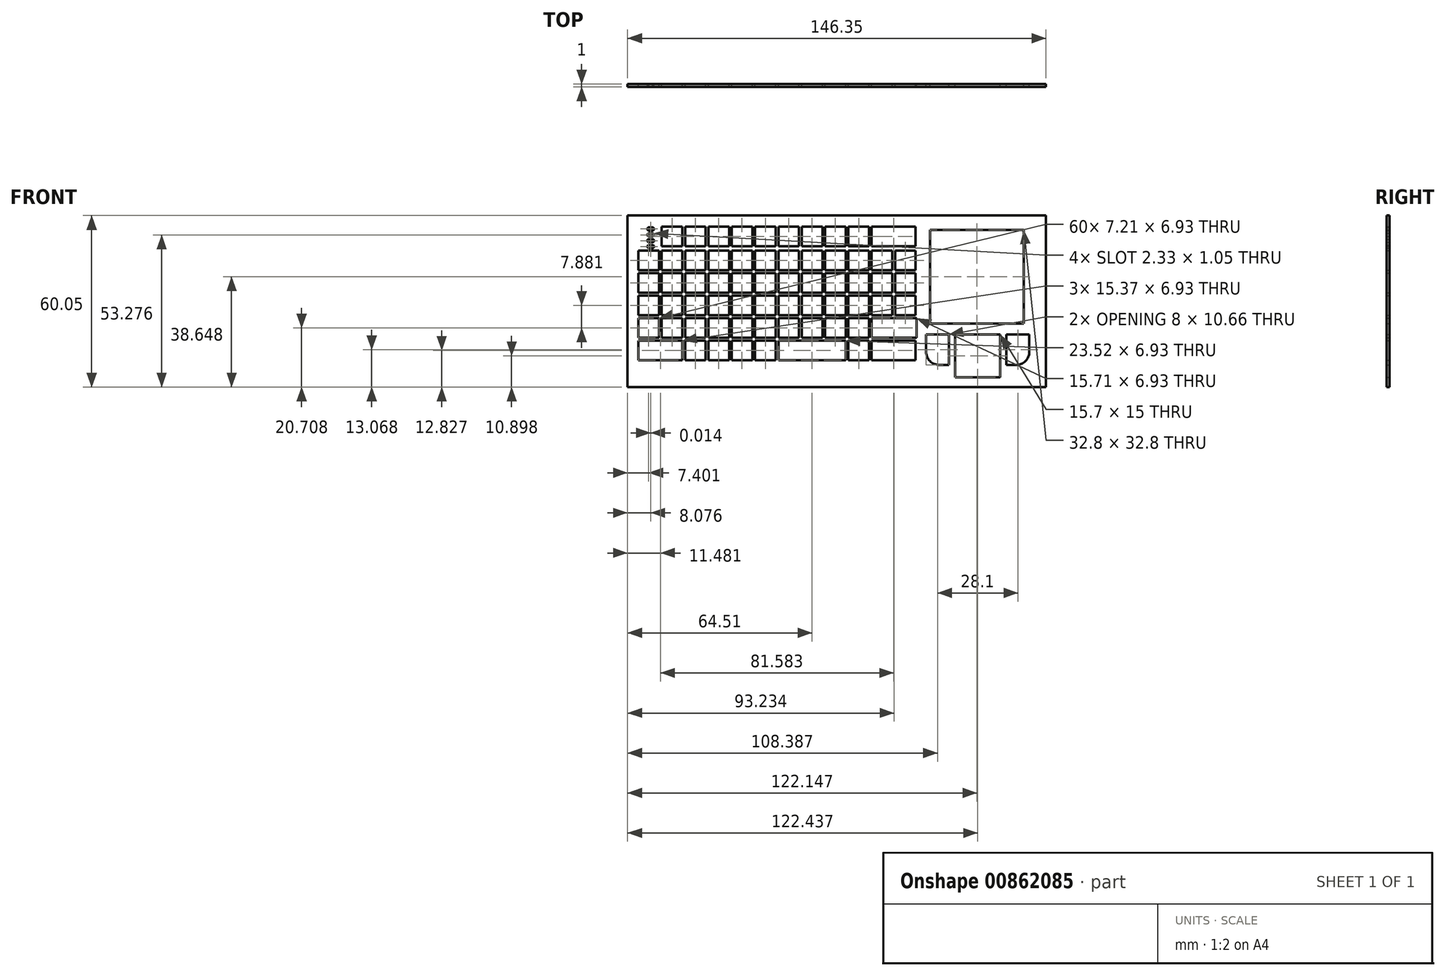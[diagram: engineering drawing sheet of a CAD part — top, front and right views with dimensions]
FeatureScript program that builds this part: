
annotation { "Feature Type Name" : "Feature", "Feature Type Description" : "" }
export const myFeature = defineFeature(function(context is Context, id is Id, definition is map)
    precondition{}
    {
        {
            var Q0;
            Q0=qCreatedBy(makeId("Front.planeOp"),FACE);
            var sketch = newSketch(context, id + "F0", { "sketchPlane" : qUnion([Q0])});
            skLineSegment(sketch, "E0.bottom", {"start": v(-58.57, 14.86) * mm, "end": v(-51.36, 14.86) * mm});
            skLineSegment(sketch, "E0.top", {"start": v(-58.57, 7.93) * mm, "end": v(-51.36, 7.93) * mm});
            skLineSegment(sketch, "E0.left", {"start": v(-58.57, 14.86) * mm, "end": v(-58.57, 7.93) * mm});
            skLineSegment(sketch, "E0.right", {"start": v(-51.36, 14.86) * mm, "end": v(-51.36, 7.93) * mm});
            skLineSegment(sketch, "E1.bottom", {"start": v(-50.41, 14.86) * mm, "end": v(-43.2, 14.86) * mm});
            skLineSegment(sketch, "E1.top", {"start": v(-50.41, 7.93) * mm, "end": v(-43.2, 7.93) * mm});
            skLineSegment(sketch, "E1.left", {"start": v(-50.41, 14.86) * mm, "end": v(-50.41, 7.93) * mm});
            skLineSegment(sketch, "E1.right", {"start": v(-43.2, 14.86) * mm, "end": v(-43.2, 7.93) * mm});
            skLineSegment(sketch, "E2.bottom", {"start": v(-42.26, 14.86) * mm, "end": v(-35.05, 14.86) * mm});
            skLineSegment(sketch, "E2.top", {"start": v(-42.26, 7.93) * mm, "end": v(-35.05, 7.93) * mm});
            skLineSegment(sketch, "E2.left", {"start": v(-42.26, 14.86) * mm, "end": v(-42.26, 7.93) * mm});
            skLineSegment(sketch, "E2.right", {"start": v(-35.05, 14.86) * mm, "end": v(-35.05, 7.93) * mm});
            skLineSegment(sketch, "E3.bottom", {"start": v(-34.1, 14.86) * mm, "end": v(-26.89, 14.86) * mm});
            skLineSegment(sketch, "E3.top", {"start": v(-34.1, 7.93) * mm, "end": v(-26.89, 7.93) * mm});
            skLineSegment(sketch, "E3.left", {"start": v(-34.1, 14.86) * mm, "end": v(-34.1, 7.93) * mm});
            skLineSegment(sketch, "E3.right", {"start": v(-26.89, 14.86) * mm, "end": v(-26.89, 7.93) * mm});
            skLineSegment(sketch, "E4.bottom", {"start": v(-25.94, 14.86) * mm, "end": v(-18.73, 14.86) * mm});
            skLineSegment(sketch, "E4.top", {"start": v(-25.94, 7.93) * mm, "end": v(-18.73, 7.93) * mm});
            skLineSegment(sketch, "E4.left", {"start": v(-25.94, 14.86) * mm, "end": v(-25.94, 7.93) * mm});
            skLineSegment(sketch, "E4.right", {"start": v(-18.73, 14.86) * mm, "end": v(-18.73, 7.93) * mm});
            skLineSegment(sketch, "E5.bottom", {"start": v(-17.78, 14.86) * mm, "end": v(-10.57, 14.86) * mm});
            skLineSegment(sketch, "E5.top", {"start": v(-17.78, 7.93) * mm, "end": v(-10.57, 7.93) * mm});
            skLineSegment(sketch, "E5.left", {"start": v(-17.78, 14.86) * mm, "end": v(-17.78, 7.93) * mm});
            skLineSegment(sketch, "E5.right", {"start": v(-10.57, 14.86) * mm, "end": v(-10.57, 7.93) * mm});
            skLineSegment(sketch, "E6.bottom", {"start": v(-9.62, 14.86) * mm, "end": v(-2.41, 14.86) * mm});
            skLineSegment(sketch, "E6.top", {"start": v(-9.62, 7.93) * mm, "end": v(-2.41, 7.93) * mm});
            skLineSegment(sketch, "E6.left", {"start": v(-9.62, 14.86) * mm, "end": v(-9.62, 7.93) * mm});
            skLineSegment(sketch, "E6.right", {"start": v(-2.41, 14.86) * mm, "end": v(-2.41, 7.93) * mm});
            skLineSegment(sketch, "E7.bottom", {"start": v(-1.46, 14.86) * mm, "end": v(5.74, 14.86) * mm});
            skLineSegment(sketch, "E7.top", {"start": v(-1.46, 7.93) * mm, "end": v(5.74, 7.93) * mm});
            skLineSegment(sketch, "E7.left", {"start": v(-1.46, 14.86) * mm, "end": v(-1.46, 7.93) * mm});
            skLineSegment(sketch, "E7.right", {"start": v(5.74, 14.86) * mm, "end": v(5.74, 7.93) * mm});
            skLineSegment(sketch, "E8.bottom", {"start": v(6.7, 14.86) * mm, "end": v(13.9, 14.86) * mm});
            skLineSegment(sketch, "E8.top", {"start": v(6.7, 7.93) * mm, "end": v(13.9, 7.93) * mm});
            skLineSegment(sketch, "E8.left", {"start": v(6.7, 14.86) * mm, "end": v(6.7, 7.93) * mm});
            skLineSegment(sketch, "E8.right", {"start": v(13.9, 14.86) * mm, "end": v(13.9, 7.93) * mm});
            skLineSegment(sketch, "E9.bottom", {"start": v(14.85, 14.86) * mm, "end": v(22.06, 14.86) * mm});
            skLineSegment(sketch, "E9.top", {"start": v(14.85, 7.93) * mm, "end": v(22.06, 7.93) * mm});
            skLineSegment(sketch, "E9.left", {"start": v(14.85, 14.86) * mm, "end": v(14.85, 7.93) * mm});
            skLineSegment(sketch, "E9.right", {"start": v(22.06, 14.86) * mm, "end": v(22.06, 7.93) * mm});
            skLineSegment(sketch, "E10.bottom", {"start": v(23.01, 14.86) * mm, "end": v(30.22, 14.86) * mm});
            skLineSegment(sketch, "E10.top", {"start": v(23.01, 7.93) * mm, "end": v(30.22, 7.93) * mm});
            skLineSegment(sketch, "E10.left", {"start": v(23.01, 14.86) * mm, "end": v(23.01, 7.93) * mm});
            skLineSegment(sketch, "E10.right", {"start": v(30.22, 14.86) * mm, "end": v(30.22, 7.93) * mm});
            skLineSegment(sketch, "E11.bottom", {"start": v(31.17, 14.86) * mm, "end": v(38.38, 14.86) * mm});
            skLineSegment(sketch, "E11.top", {"start": v(31.17, 7.93) * mm, "end": v(38.38, 7.93) * mm});
            skLineSegment(sketch, "E11.left", {"start": v(31.17, 14.86) * mm, "end": v(31.17, 7.93) * mm});
            skLineSegment(sketch, "E11.right", {"start": v(38.38, 14.86) * mm, "end": v(38.38, 7.93) * mm});
            skLineSegment(sketch, "E12", {"start": v(-58.57, 7.93) * mm, "end": v(38.38, 7.93) * mm});
            skLineSegment(sketch, "E13", {"start": v(-58.57, 14.86) * mm, "end": v(38.38, 14.86) * mm});
            skLineSegment(sketch, "E14.bottom", {"start": v(-58.57, 6.98) * mm, "end": v(-51.36, 6.98) * mm});
            skLineSegment(sketch, "E14.top", {"start": v(-58.57, 0.04) * mm, "end": v(-51.36, 0.04) * mm});
            skLineSegment(sketch, "E14.left", {"start": v(-58.57, 6.98) * mm, "end": v(-58.57, 0.04) * mm});
            skLineSegment(sketch, "E14.right", {"start": v(-51.36, 6.98) * mm, "end": v(-51.36, 0.04) * mm});
            skLineSegment(sketch, "E15.bottom", {"start": v(-50.41, 6.98) * mm, "end": v(-43.2, 6.98) * mm});
            skLineSegment(sketch, "E15.top", {"start": v(-50.41, 0.04) * mm, "end": v(-43.2, 0.04) * mm});
            skLineSegment(sketch, "E15.left", {"start": v(-50.41, 6.98) * mm, "end": v(-50.41, 0.04) * mm});
            skLineSegment(sketch, "E15.right", {"start": v(-43.2, 6.98) * mm, "end": v(-43.2, 0.04) * mm});
            skLineSegment(sketch, "E16.bottom", {"start": v(-42.26, 6.98) * mm, "end": v(-35.05, 6.98) * mm});
            skLineSegment(sketch, "E16.top", {"start": v(-42.26, 0.04) * mm, "end": v(-35.05, 0.04) * mm});
            skLineSegment(sketch, "E16.left", {"start": v(-42.26, 6.98) * mm, "end": v(-42.26, 0.04) * mm});
            skLineSegment(sketch, "E16.right", {"start": v(-35.05, 6.98) * mm, "end": v(-35.05, 0.04) * mm});
            skLineSegment(sketch, "E17.bottom", {"start": v(-34.1, 6.98) * mm, "end": v(-26.89, 6.98) * mm});
            skLineSegment(sketch, "E17.top", {"start": v(-34.1, 0.04) * mm, "end": v(-26.89, 0.04) * mm});
            skLineSegment(sketch, "E17.left", {"start": v(-34.1, 6.98) * mm, "end": v(-34.1, 0.04) * mm});
            skLineSegment(sketch, "E17.right", {"start": v(-26.89, 6.98) * mm, "end": v(-26.89, 0.04) * mm});
            skLineSegment(sketch, "E18.bottom", {"start": v(-25.94, 6.98) * mm, "end": v(-18.73, 6.98) * mm});
            skLineSegment(sketch, "E18.top", {"start": v(-25.94, 0.04) * mm, "end": v(-18.73, 0.04) * mm});
            skLineSegment(sketch, "E18.left", {"start": v(-25.94, 6.98) * mm, "end": v(-25.94, 0.04) * mm});
            skLineSegment(sketch, "E18.right", {"start": v(-18.73, 6.98) * mm, "end": v(-18.73, 0.04) * mm});
            skLineSegment(sketch, "E19.bottom", {"start": v(-17.78, 6.98) * mm, "end": v(-10.57, 6.98) * mm});
            skLineSegment(sketch, "E19.top", {"start": v(-17.78, 0.04) * mm, "end": v(-10.57, 0.04) * mm});
            skLineSegment(sketch, "E19.left", {"start": v(-17.78, 6.98) * mm, "end": v(-17.78, 0.04) * mm});
            skLineSegment(sketch, "E19.right", {"start": v(-10.57, 6.98) * mm, "end": v(-10.57, 0.04) * mm});
            skLineSegment(sketch, "E20.bottom", {"start": v(-9.62, 6.98) * mm, "end": v(-2.41, 6.98) * mm});
            skLineSegment(sketch, "E20.top", {"start": v(-9.62, 0.04) * mm, "end": v(-2.41, 0.04) * mm});
            skLineSegment(sketch, "E20.left", {"start": v(-9.62, 6.98) * mm, "end": v(-9.62, 0.04) * mm});
            skLineSegment(sketch, "E20.right", {"start": v(-2.41, 6.98) * mm, "end": v(-2.41, 0.04) * mm});
            skLineSegment(sketch, "E21.bottom", {"start": v(-1.46, 6.98) * mm, "end": v(5.74, 6.98) * mm});
            skLineSegment(sketch, "E21.top", {"start": v(-1.46, 0.04) * mm, "end": v(5.74, 0.04) * mm});
            skLineSegment(sketch, "E21.left", {"start": v(-1.46, 6.98) * mm, "end": v(-1.46, 0.04) * mm});
            skLineSegment(sketch, "E21.right", {"start": v(5.74, 6.98) * mm, "end": v(5.74, 0.04) * mm});
            skLineSegment(sketch, "E22.bottom", {"start": v(6.7, 6.98) * mm, "end": v(13.9, 6.98) * mm});
            skLineSegment(sketch, "E22.top", {"start": v(6.7, 0.04) * mm, "end": v(13.9, 0.04) * mm});
            skLineSegment(sketch, "E22.left", {"start": v(6.7, 6.98) * mm, "end": v(6.7, 0.04) * mm});
            skLineSegment(sketch, "E22.right", {"start": v(13.9, 6.98) * mm, "end": v(13.9, 0.04) * mm});
            skLineSegment(sketch, "E23.bottom", {"start": v(14.85, 6.98) * mm, "end": v(22.06, 6.98) * mm});
            skLineSegment(sketch, "E23.top", {"start": v(14.85, 0.04) * mm, "end": v(22.06, 0.04) * mm});
            skLineSegment(sketch, "E23.left", {"start": v(14.85, 6.98) * mm, "end": v(14.85, 0.04) * mm});
            skLineSegment(sketch, "E23.right", {"start": v(22.06, 6.98) * mm, "end": v(22.06, 0.04) * mm});
            skLineSegment(sketch, "E24.bottom", {"start": v(23.01, 6.98) * mm, "end": v(30.22, 6.98) * mm});
            skLineSegment(sketch, "E24.top", {"start": v(23.01, 0.04) * mm, "end": v(30.22, 0.04) * mm});
            skLineSegment(sketch, "E24.left", {"start": v(23.01, 6.98) * mm, "end": v(23.01, 0.04) * mm});
            skLineSegment(sketch, "E24.right", {"start": v(30.22, 6.98) * mm, "end": v(30.22, 0.04) * mm});
            skLineSegment(sketch, "E25.bottom", {"start": v(31.17, 6.98) * mm, "end": v(38.38, 6.98) * mm});
            skLineSegment(sketch, "E25.top", {"start": v(31.17, 0.04) * mm, "end": v(38.38, 0.04) * mm});
            skLineSegment(sketch, "E25.left", {"start": v(31.17, 6.98) * mm, "end": v(31.17, 0.04) * mm});
            skLineSegment(sketch, "E25.right", {"start": v(38.38, 6.98) * mm, "end": v(38.38, 0.04) * mm});
            skLineSegment(sketch, "E26", {"start": v(-58.57, 0.04) * mm, "end": v(38.38, 0.04) * mm});
            skLineSegment(sketch, "E27", {"start": v(-58.57, 6.98) * mm, "end": v(38.38, 6.98) * mm});
            skLineSegment(sketch, "E28.bottom", {"start": v(-58.57, -0.9) * mm, "end": v(-51.36, -0.9) * mm});
            skLineSegment(sketch, "E28.top", {"start": v(-58.57, -7.84) * mm, "end": v(-51.36, -7.84) * mm});
            skLineSegment(sketch, "E28.left", {"start": v(-58.57, -0.9) * mm, "end": v(-58.57, -7.84) * mm});
            skLineSegment(sketch, "E28.right", {"start": v(-51.36, -0.9) * mm, "end": v(-51.36, -7.84) * mm});
            skLineSegment(sketch, "E29.bottom", {"start": v(-50.41, -0.9) * mm, "end": v(-43.2, -0.9) * mm});
            skLineSegment(sketch, "E29.top", {"start": v(-50.41, -7.84) * mm, "end": v(-43.2, -7.84) * mm});
            skLineSegment(sketch, "E29.left", {"start": v(-50.41, -0.9) * mm, "end": v(-50.41, -7.84) * mm});
            skLineSegment(sketch, "E29.right", {"start": v(-43.2, -0.9) * mm, "end": v(-43.2, -7.84) * mm});
            skLineSegment(sketch, "E30.bottom", {"start": v(-42.26, -0.9) * mm, "end": v(-35.05, -0.9) * mm});
            skLineSegment(sketch, "E30.top", {"start": v(-42.26, -7.84) * mm, "end": v(-35.05, -7.84) * mm});
            skLineSegment(sketch, "E30.left", {"start": v(-42.26, -0.9) * mm, "end": v(-42.26, -7.84) * mm});
            skLineSegment(sketch, "E30.right", {"start": v(-35.05, -0.9) * mm, "end": v(-35.05, -7.84) * mm});
            skLineSegment(sketch, "E31.bottom", {"start": v(-34.1, -0.9) * mm, "end": v(-26.89, -0.9) * mm});
            skLineSegment(sketch, "E31.top", {"start": v(-34.1, -7.84) * mm, "end": v(-26.89, -7.84) * mm});
            skLineSegment(sketch, "E31.left", {"start": v(-34.1, -0.9) * mm, "end": v(-34.1, -7.84) * mm});
            skLineSegment(sketch, "E31.right", {"start": v(-26.89, -0.9) * mm, "end": v(-26.89, -7.84) * mm});
            skLineSegment(sketch, "E32.bottom", {"start": v(-25.94, -0.9) * mm, "end": v(-18.73, -0.9) * mm});
            skLineSegment(sketch, "E32.top", {"start": v(-25.94, -7.84) * mm, "end": v(-18.73, -7.84) * mm});
            skLineSegment(sketch, "E32.left", {"start": v(-25.94, -0.9) * mm, "end": v(-25.94, -7.84) * mm});
            skLineSegment(sketch, "E32.right", {"start": v(-18.73, -0.9) * mm, "end": v(-18.73, -7.84) * mm});
            skLineSegment(sketch, "E33.bottom", {"start": v(-17.78, -0.9) * mm, "end": v(-10.57, -0.9) * mm});
            skLineSegment(sketch, "E33.top", {"start": v(-17.78, -7.84) * mm, "end": v(-10.57, -7.84) * mm});
            skLineSegment(sketch, "E33.left", {"start": v(-17.78, -0.9) * mm, "end": v(-17.78, -7.84) * mm});
            skLineSegment(sketch, "E33.right", {"start": v(-10.57, -0.9) * mm, "end": v(-10.57, -7.84) * mm});
            skLineSegment(sketch, "E34.bottom", {"start": v(-9.62, -0.9) * mm, "end": v(-2.41, -0.9) * mm});
            skLineSegment(sketch, "E34.top", {"start": v(-9.62, -7.84) * mm, "end": v(-2.41, -7.84) * mm});
            skLineSegment(sketch, "E34.left", {"start": v(-9.62, -0.9) * mm, "end": v(-9.62, -7.84) * mm});
            skLineSegment(sketch, "E34.right", {"start": v(-2.41, -0.9) * mm, "end": v(-2.41, -7.84) * mm});
            skLineSegment(sketch, "E35.bottom", {"start": v(-1.46, -0.9) * mm, "end": v(5.74, -0.9) * mm});
            skLineSegment(sketch, "E35.top", {"start": v(-1.46, -7.84) * mm, "end": v(5.74, -7.84) * mm});
            skLineSegment(sketch, "E35.left", {"start": v(-1.46, -0.9) * mm, "end": v(-1.46, -7.84) * mm});
            skLineSegment(sketch, "E35.right", {"start": v(5.74, -0.9) * mm, "end": v(5.74, -7.84) * mm});
            skLineSegment(sketch, "E36.bottom", {"start": v(6.7, -0.9) * mm, "end": v(13.9, -0.9) * mm});
            skLineSegment(sketch, "E36.top", {"start": v(6.7, -7.84) * mm, "end": v(13.9, -7.84) * mm});
            skLineSegment(sketch, "E36.left", {"start": v(6.7, -0.9) * mm, "end": v(6.7, -7.84) * mm});
            skLineSegment(sketch, "E36.right", {"start": v(13.9, -0.9) * mm, "end": v(13.9, -7.84) * mm});
            skLineSegment(sketch, "E37.bottom", {"start": v(14.85, -0.9) * mm, "end": v(22.06, -0.9) * mm});
            skLineSegment(sketch, "E37.top", {"start": v(14.85, -7.84) * mm, "end": v(22.06, -7.84) * mm});
            skLineSegment(sketch, "E37.left", {"start": v(14.85, -0.9) * mm, "end": v(14.85, -7.84) * mm});
            skLineSegment(sketch, "E37.right", {"start": v(22.06, -0.9) * mm, "end": v(22.06, -7.84) * mm});
            skLineSegment(sketch, "E38.bottom", {"start": v(23.01, -0.9) * mm, "end": v(30.22, -0.9) * mm});
            skLineSegment(sketch, "E38.top", {"start": v(23.01, -7.84) * mm, "end": v(30.22, -7.84) * mm});
            skLineSegment(sketch, "E38.left", {"start": v(23.01, -0.9) * mm, "end": v(23.01, -7.84) * mm});
            skLineSegment(sketch, "E38.right", {"start": v(30.22, -0.9) * mm, "end": v(30.22, -7.84) * mm});
            skLineSegment(sketch, "E39.bottom", {"start": v(31.17, -0.9) * mm, "end": v(38.38, -0.9) * mm});
            skLineSegment(sketch, "E39.top", {"start": v(31.17, -7.84) * mm, "end": v(38.38, -7.84) * mm});
            skLineSegment(sketch, "E39.left", {"start": v(31.17, -0.9) * mm, "end": v(31.17, -7.84) * mm});
            skLineSegment(sketch, "E39.right", {"start": v(38.38, -0.9) * mm, "end": v(38.38, -7.84) * mm});
            skLineSegment(sketch, "E40", {"start": v(-58.57, -7.84) * mm, "end": v(38.38, -7.84) * mm});
            skLineSegment(sketch, "E41", {"start": v(-58.57, -0.9) * mm, "end": v(38.38, -0.9) * mm});
            skLineSegment(sketch, "E42.bottom", {"start": v(-58.57, -8.79) * mm, "end": v(-51.36, -8.79) * mm});
            skLineSegment(sketch, "E42.top", {"start": v(-58.57, -15.72) * mm, "end": v(-51.36, -15.72) * mm});
            skLineSegment(sketch, "E42.left", {"start": v(-58.57, -8.79) * mm, "end": v(-58.57, -15.72) * mm});
            skLineSegment(sketch, "E42.right", {"start": v(-51.36, -8.79) * mm, "end": v(-51.36, -15.72) * mm});
            skLineSegment(sketch, "E43.bottom", {"start": v(-50.41, -8.79) * mm, "end": v(-43.2, -8.79) * mm});
            skLineSegment(sketch, "E43.top", {"start": v(-50.41, -15.72) * mm, "end": v(-43.2, -15.72) * mm});
            skLineSegment(sketch, "E43.left", {"start": v(-50.41, -8.79) * mm, "end": v(-50.41, -15.72) * mm});
            skLineSegment(sketch, "E43.right", {"start": v(-43.2, -8.79) * mm, "end": v(-43.2, -15.72) * mm});
            skLineSegment(sketch, "E44.bottom", {"start": v(-42.26, -8.79) * mm, "end": v(-35.05, -8.79) * mm});
            skLineSegment(sketch, "E44.top", {"start": v(-42.26, -15.72) * mm, "end": v(-35.05, -15.72) * mm});
            skLineSegment(sketch, "E44.left", {"start": v(-42.26, -8.79) * mm, "end": v(-42.26, -15.72) * mm});
            skLineSegment(sketch, "E44.right", {"start": v(-35.05, -8.79) * mm, "end": v(-35.05, -15.72) * mm});
            skLineSegment(sketch, "E45.bottom", {"start": v(-34.1, -8.79) * mm, "end": v(-26.89, -8.79) * mm});
            skLineSegment(sketch, "E45.top", {"start": v(-34.1, -15.72) * mm, "end": v(-26.89, -15.72) * mm});
            skLineSegment(sketch, "E45.left", {"start": v(-34.1, -8.79) * mm, "end": v(-34.1, -15.72) * mm});
            skLineSegment(sketch, "E45.right", {"start": v(-26.89, -8.79) * mm, "end": v(-26.89, -15.72) * mm});
            skLineSegment(sketch, "E46.bottom", {"start": v(-25.94, -8.79) * mm, "end": v(-18.73, -8.79) * mm});
            skLineSegment(sketch, "E46.top", {"start": v(-25.94, -15.72) * mm, "end": v(-18.73, -15.72) * mm});
            skLineSegment(sketch, "E46.left", {"start": v(-25.94, -8.79) * mm, "end": v(-25.94, -15.72) * mm});
            skLineSegment(sketch, "E46.right", {"start": v(-18.73, -8.79) * mm, "end": v(-18.73, -15.72) * mm});
            skLineSegment(sketch, "E47.bottom", {"start": v(-17.78, -8.79) * mm, "end": v(-10.57, -8.79) * mm});
            skLineSegment(sketch, "E47.top", {"start": v(-17.78, -15.72) * mm, "end": v(-10.57, -15.72) * mm});
            skLineSegment(sketch, "E47.left", {"start": v(-17.78, -8.79) * mm, "end": v(-17.78, -15.72) * mm});
            skLineSegment(sketch, "E47.right", {"start": v(-10.57, -8.79) * mm, "end": v(-10.57, -15.72) * mm});
            skLineSegment(sketch, "E48.bottom", {"start": v(-9.62, -8.79) * mm, "end": v(-2.41, -8.79) * mm});
            skLineSegment(sketch, "E48.top", {"start": v(-9.62, -15.72) * mm, "end": v(-2.41, -15.72) * mm});
            skLineSegment(sketch, "E48.left", {"start": v(-9.62, -8.79) * mm, "end": v(-9.62, -15.72) * mm});
            skLineSegment(sketch, "E48.right", {"start": v(-2.41, -8.79) * mm, "end": v(-2.41, -15.72) * mm});
            skLineSegment(sketch, "E49.bottom", {"start": v(-1.46, -8.79) * mm, "end": v(5.74, -8.79) * mm});
            skLineSegment(sketch, "E49.top", {"start": v(-1.46, -15.72) * mm, "end": v(5.74, -15.72) * mm});
            skLineSegment(sketch, "E49.left", {"start": v(-1.46, -8.79) * mm, "end": v(-1.46, -15.72) * mm});
            skLineSegment(sketch, "E49.right", {"start": v(5.74, -8.79) * mm, "end": v(5.74, -15.72) * mm});
            skLineSegment(sketch, "E50.bottom", {"start": v(6.7, -8.79) * mm, "end": v(13.9, -8.79) * mm});
            skLineSegment(sketch, "E50.top", {"start": v(6.7, -15.72) * mm, "end": v(13.9, -15.72) * mm});
            skLineSegment(sketch, "E50.left", {"start": v(6.7, -8.79) * mm, "end": v(6.7, -15.72) * mm});
            skLineSegment(sketch, "E50.right", {"start": v(13.9, -8.79) * mm, "end": v(13.9, -15.72) * mm});
            skLineSegment(sketch, "E51.bottom", {"start": v(14.85, -8.79) * mm, "end": v(22.06, -8.79) * mm});
            skLineSegment(sketch, "E51.top", {"start": v(14.85, -15.72) * mm, "end": v(22.06, -15.72) * mm});
            skLineSegment(sketch, "E51.left", {"start": v(14.85, -8.79) * mm, "end": v(14.85, -15.72) * mm});
            skLineSegment(sketch, "E51.right", {"start": v(22.06, -8.79) * mm, "end": v(22.06, -15.72) * mm});
            skLineSegment(sketch, "E52.bottom", {"start": v(23.01, -8.79) * mm, "end": v(30.22, -8.79) * mm});
            skLineSegment(sketch, "E52.top", {"start": v(23.01, -15.72) * mm, "end": v(30.22, -15.72) * mm});
            skLineSegment(sketch, "E52.left", {"start": v(23.01, -8.79) * mm, "end": v(23.01, -15.72) * mm});
            skLineSegment(sketch, "E53.bottom", {"start": v(31.5, -8.79) * mm, "end": v(38.72, -8.79) * mm});
            skLineSegment(sketch, "E53.top", {"start": v(31.17, -15.72) * mm, "end": v(38.72, -15.72) * mm});
            skLineSegment(sketch, "E53.right", {"start": v(38.72, -8.79) * mm, "end": v(38.72, -15.72) * mm});
            skLineSegment(sketch, "E54", {"start": v(-58.57, -15.72) * mm, "end": v(38.72, -15.72) * mm});
            skLineSegment(sketch, "E55", {"start": v(-58.57, -8.79) * mm, "end": v(38.72, -8.79) * mm});
            skLineSegment(sketch, "E56.bottom", {"start": v(-58.57, -16.67) * mm, "end": v(-51.36, -16.67) * mm});
            skLineSegment(sketch, "E56.top", {"start": v(-56.77, -23.6) * mm, "end": v(-51.36, -23.6) * mm});
            skLineSegment(sketch, "E56.left", {"start": v(-58.57, -16.67) * mm, "end": v(-58.57, -21.8) * mm});
            skLineSegment(sketch, "E57.bottom", {"start": v(-50.41, -16.67) * mm, "end": v(-43.2, -16.67) * mm});
            skLineSegment(sketch, "E57.top", {"start": v(-50.41, -23.6) * mm, "end": v(-43.2, -23.6) * mm});
            skLineSegment(sketch, "E57.right", {"start": v(-43.2, -16.67) * mm, "end": v(-43.2, -23.6) * mm});
            skLineSegment(sketch, "E58.bottom", {"start": v(-42.26, -16.67) * mm, "end": v(-35.05, -16.67) * mm});
            skLineSegment(sketch, "E58.top", {"start": v(-42.26, -23.6) * mm, "end": v(-35.05, -23.6) * mm});
            skLineSegment(sketch, "E58.left", {"start": v(-42.26, -16.67) * mm, "end": v(-42.26, -23.6) * mm});
            skLineSegment(sketch, "E58.right", {"start": v(-35.05, -16.67) * mm, "end": v(-35.05, -23.6) * mm});
            skLineSegment(sketch, "E59.bottom", {"start": v(-34.1, -16.67) * mm, "end": v(-26.89, -16.67) * mm});
            skLineSegment(sketch, "E59.top", {"start": v(-34.1, -23.6) * mm, "end": v(-26.89, -23.6) * mm});
            skLineSegment(sketch, "E59.left", {"start": v(-34.1, -16.67) * mm, "end": v(-34.1, -23.6) * mm});
            skLineSegment(sketch, "E59.right", {"start": v(-26.89, -16.67) * mm, "end": v(-26.89, -23.6) * mm});
            skLineSegment(sketch, "E60.bottom", {"start": v(-25.94, -16.67) * mm, "end": v(-18.73, -16.67) * mm});
            skLineSegment(sketch, "E60.top", {"start": v(-25.94, -23.6) * mm, "end": v(-18.73, -23.6) * mm});
            skLineSegment(sketch, "E60.left", {"start": v(-25.94, -16.67) * mm, "end": v(-25.94, -23.6) * mm});
            skLineSegment(sketch, "E60.right", {"start": v(-18.73, -16.67) * mm, "end": v(-18.73, -23.6) * mm});
            skLineSegment(sketch, "E61.bottom", {"start": v(-17.78, -16.67) * mm, "end": v(-10.57, -16.67) * mm});
            skLineSegment(sketch, "E61.top", {"start": v(-17.78, -23.6) * mm, "end": v(-10.57, -23.6) * mm});
            skLineSegment(sketch, "E61.left", {"start": v(-17.78, -16.67) * mm, "end": v(-17.78, -23.6) * mm});
            skLineSegment(sketch, "E61.right", {"start": v(-10.57, -16.67) * mm, "end": v(-10.57, -23.6) * mm});
            skLineSegment(sketch, "E62.bottom", {"start": v(-9.62, -16.67) * mm, "end": v(-2.41, -16.67) * mm});
            skLineSegment(sketch, "E62.top", {"start": v(-9.62, -23.6) * mm, "end": v(-2.41, -23.6) * mm});
            skLineSegment(sketch, "E62.left", {"start": v(-9.62, -16.67) * mm, "end": v(-9.62, -23.6) * mm});
            skLineSegment(sketch, "E63.bottom", {"start": v(-1.46, -16.67) * mm, "end": v(5.74, -16.67) * mm});
            skLineSegment(sketch, "E63.top", {"start": v(-1.46, -23.6) * mm, "end": v(5.74, -23.6) * mm});
            skLineSegment(sketch, "E64.bottom", {"start": v(6.7, -16.67) * mm, "end": v(13.9, -16.67) * mm});
            skLineSegment(sketch, "E64.top", {"start": v(6.7, -23.6) * mm, "end": v(13.9, -23.6) * mm});
            skLineSegment(sketch, "E64.right", {"start": v(13.9, -16.67) * mm, "end": v(13.9, -23.6) * mm});
            skLineSegment(sketch, "E65.bottom", {"start": v(14.85, -16.67) * mm, "end": v(22.06, -16.67) * mm});
            skLineSegment(sketch, "E65.top", {"start": v(14.85, -23.6) * mm, "end": v(22.06, -23.6) * mm});
            skLineSegment(sketch, "E65.left", {"start": v(14.85, -16.67) * mm, "end": v(14.85, -23.6) * mm});
            skLineSegment(sketch, "E65.right", {"start": v(22.06, -16.67) * mm, "end": v(22.06, -23.6) * mm});
            skLineSegment(sketch, "E66.bottom", {"start": v(23.01, -16.67) * mm, "end": v(30.22, -16.67) * mm});
            skLineSegment(sketch, "E66.top", {"start": v(23.01, -23.6) * mm, "end": v(30.22, -23.6) * mm});
            skLineSegment(sketch, "E66.left", {"start": v(23.01, -16.67) * mm, "end": v(23.01, -23.6) * mm});
            skLineSegment(sketch, "E66.right", {"start": v(30.22, -16.67) * mm, "end": v(30.22, -23.6) * mm});
            skLineSegment(sketch, "E67.bottom", {"start": v(31.17, -16.67) * mm, "end": v(38.38, -16.67) * mm});
            skLineSegment(sketch, "E67.top", {"start": v(31.17, -23.6) * mm, "end": v(38.38, -23.6) * mm});
            skLineSegment(sketch, "E67.left", {"start": v(31.17, -16.67) * mm, "end": v(31.17, -23.6) * mm});
            skLineSegment(sketch, "E67.right", {"start": v(38.38, -16.67) * mm, "end": v(38.38, -23.6) * mm});
            skLineSegment(sketch, "E68", {"start": v(-58.57, -23.6) * mm, "end": v(38.38, -23.6) * mm});
            skLineSegment(sketch, "E69", {"start": v(-58.57, -16.67) * mm, "end": v(38.38, -16.67) * mm});
            skLineSegment(sketch, "E70", {"start": v(-58.57, 14.86) * mm, "end": v(-58.57, -23.6) * mm});
            skPoint(sketch, "E71", {"position": v(-58.57, -23.6) * mm});
            skArc(sketch, "E72.filletArc", {"start": v(-58.57, -21.8) * mm, "mid": v(-58.04, -23.07) * mm, "end": v(-56.77, -23.6) * mm});
            skLineSegment(sketch, "E73.bottom", {"start": v(-50.41, 23.19) * mm, "end": v(-43.2, 23.19) * mm});
            skLineSegment(sketch, "E73.top", {"start": v(-50.41, 16.26) * mm, "end": v(-43.2, 16.26) * mm});
            skLineSegment(sketch, "E73.left", {"start": v(-50.41, 23.19) * mm, "end": v(-50.41, 16.26) * mm});
            skLineSegment(sketch, "E73.right", {"start": v(-43.2, 23.19) * mm, "end": v(-43.2, 16.26) * mm});
            skLineSegment(sketch, "E74.bottom", {"start": v(-42.26, 23.19) * mm, "end": v(-35.05, 23.19) * mm});
            skLineSegment(sketch, "E74.top", {"start": v(-42.26, 16.26) * mm, "end": v(-35.05, 16.26) * mm});
            skLineSegment(sketch, "E74.left", {"start": v(-42.26, 23.19) * mm, "end": v(-42.26, 16.26) * mm});
            skLineSegment(sketch, "E74.right", {"start": v(-35.05, 23.19) * mm, "end": v(-35.05, 16.26) * mm});
            skLineSegment(sketch, "E75.bottom", {"start": v(-34.1, 23.19) * mm, "end": v(-26.89, 23.19) * mm});
            skLineSegment(sketch, "E75.top", {"start": v(-34.1, 16.26) * mm, "end": v(-26.89, 16.26) * mm});
            skLineSegment(sketch, "E75.left", {"start": v(-34.1, 23.19) * mm, "end": v(-34.1, 16.26) * mm});
            skLineSegment(sketch, "E75.right", {"start": v(-26.89, 23.19) * mm, "end": v(-26.89, 16.26) * mm});
            skLineSegment(sketch, "E76.bottom", {"start": v(-25.94, 23.19) * mm, "end": v(-18.73, 23.19) * mm});
            skLineSegment(sketch, "E76.top", {"start": v(-25.94, 16.26) * mm, "end": v(-18.73, 16.26) * mm});
            skLineSegment(sketch, "E76.left", {"start": v(-25.94, 23.19) * mm, "end": v(-25.94, 16.26) * mm});
            skLineSegment(sketch, "E76.right", {"start": v(-18.73, 23.19) * mm, "end": v(-18.73, 16.26) * mm});
            skLineSegment(sketch, "E77.bottom", {"start": v(-17.78, 23.19) * mm, "end": v(-10.57, 23.19) * mm});
            skLineSegment(sketch, "E77.top", {"start": v(-17.78, 16.26) * mm, "end": v(-10.57, 16.26) * mm});
            skLineSegment(sketch, "E77.left", {"start": v(-17.78, 23.19) * mm, "end": v(-17.78, 16.26) * mm});
            skLineSegment(sketch, "E77.right", {"start": v(-10.57, 23.19) * mm, "end": v(-10.57, 16.26) * mm});
            skLineSegment(sketch, "E78.bottom", {"start": v(-9.62, 23.19) * mm, "end": v(-2.41, 23.19) * mm});
            skLineSegment(sketch, "E78.top", {"start": v(-9.62, 16.26) * mm, "end": v(-2.41, 16.26) * mm});
            skLineSegment(sketch, "E78.left", {"start": v(-9.62, 23.19) * mm, "end": v(-9.62, 16.26) * mm});
            skLineSegment(sketch, "E78.right", {"start": v(-2.41, 23.19) * mm, "end": v(-2.41, 16.26) * mm});
            skLineSegment(sketch, "E79.bottom", {"start": v(-1.46, 23.19) * mm, "end": v(5.74, 23.19) * mm});
            skLineSegment(sketch, "E79.top", {"start": v(-1.46, 16.26) * mm, "end": v(5.74, 16.26) * mm});
            skLineSegment(sketch, "E79.left", {"start": v(-1.46, 23.19) * mm, "end": v(-1.46, 16.26) * mm});
            skLineSegment(sketch, "E79.right", {"start": v(5.74, 23.19) * mm, "end": v(5.74, 16.26) * mm});
            skLineSegment(sketch, "E80.bottom", {"start": v(6.7, 23.19) * mm, "end": v(13.9, 23.19) * mm});
            skLineSegment(sketch, "E80.top", {"start": v(6.7, 16.26) * mm, "end": v(13.9, 16.26) * mm});
            skLineSegment(sketch, "E80.left", {"start": v(6.7, 23.19) * mm, "end": v(6.7, 16.26) * mm});
            skLineSegment(sketch, "E80.right", {"start": v(13.9, 23.19) * mm, "end": v(13.9, 16.26) * mm});
            skLineSegment(sketch, "E81.bottom", {"start": v(14.85, 23.19) * mm, "end": v(22.06, 23.19) * mm});
            skLineSegment(sketch, "E81.top", {"start": v(14.85, 16.26) * mm, "end": v(22.06, 16.26) * mm});
            skLineSegment(sketch, "E81.left", {"start": v(14.85, 23.19) * mm, "end": v(14.85, 16.26) * mm});
            skLineSegment(sketch, "E81.right", {"start": v(22.06, 23.19) * mm, "end": v(22.06, 16.26) * mm});
            skLineSegment(sketch, "E82.bottom", {"start": v(23.01, 23.19) * mm, "end": v(30.22, 23.19) * mm});
            skLineSegment(sketch, "E82.top", {"start": v(23.01, 16.26) * mm, "end": v(30.22, 16.26) * mm});
            skLineSegment(sketch, "E82.left", {"start": v(23.01, 23.19) * mm, "end": v(23.01, 16.26) * mm});
            skLineSegment(sketch, "E83.bottom", {"start": v(31.17, 23.19) * mm, "end": v(38.38, 23.19) * mm});
            skLineSegment(sketch, "E83.top", {"start": v(31.17, 16.26) * mm, "end": v(38.38, 16.26) * mm});
            skLineSegment(sketch, "E83.right", {"start": v(38.38, 23.19) * mm, "end": v(38.38, 16.26) * mm});
            skLineSegment(sketch, "E84", {"start": v(-50.41, 16.26) * mm, "end": v(38.38, 16.26) * mm});
            skLineSegment(sketch, "E85", {"start": v(-50.41, 23.19) * mm, "end": v(38.38, 23.19) * mm});
            skLineSegment(sketch, "E86.bottom", {"start": v(43.38, 22.09) * mm, "end": v(76.18, 22.09) * mm});
            skLineSegment(sketch, "E86.top", {"start": v(43.38, -10.71) * mm, "end": v(76.18, -10.71) * mm});
            skLineSegment(sketch, "E86.left", {"start": v(43.38, 22.09) * mm, "end": v(43.38, -10.71) * mm});
            skLineSegment(sketch, "E86.right", {"start": v(76.18, 22.09) * mm, "end": v(76.18, -10.71) * mm});
            skLineSegment(sketch, "E87", {"start": v(-62.37, 27.09) * mm, "end": v(83.98, 27.09) * mm});
            skLineSegment(sketch, "E88.bottom", {"start": v(42.02, -14.56) * mm, "end": v(50.02, -14.56) * mm});
            skLineSegment(sketch, "E88.top", {"start": v(46.68, -25.22) * mm, "end": v(50.02, -25.22) * mm});
            skLineSegment(sketch, "E88.left", {"start": v(42.02, -14.56) * mm, "end": v(42.02, -20.56) * mm});
            skLineSegment(sketch, "E88.right", {"start": v(50.02, -14.56) * mm, "end": v(50.02, -25.22) * mm});
            skLineSegment(sketch, "E89.bottom", {"start": v(52.22, -14.56) * mm, "end": v(67.92, -14.56) * mm});
            skLineSegment(sketch, "E89.top", {"start": v(52.22, -29.56) * mm, "end": v(67.92, -29.56) * mm});
            skLineSegment(sketch, "E89.left", {"start": v(52.22, -14.56) * mm, "end": v(52.22, -29.56) * mm});
            skLineSegment(sketch, "E89.right", {"start": v(67.92, -14.56) * mm, "end": v(67.92, -29.56) * mm});
            skLineSegment(sketch, "E90", {"start": v(42.02, -14.56) * mm, "end": v(78.12, -14.56) * mm});
            skLineSegment(sketch, "E91.bottom", {"start": v(70.12, -14.56) * mm, "end": v(78.12, -14.56) * mm});
            skLineSegment(sketch, "E91.top", {"start": v(70.12, -25.22) * mm, "end": v(73.46, -25.22) * mm});
            skLineSegment(sketch, "E91.left", {"start": v(70.12, -14.56) * mm, "end": v(70.12, -25.22) * mm});
            skLineSegment(sketch, "E91.right", {"start": v(78.12, -14.56) * mm, "end": v(78.12, -20.56) * mm});
            skPoint(sketch, "E92.visualSharp", {"position": v(42.02, -25.22) * mm});
            skArc(sketch, "E92.filletArc", {"start": v(42.02, -20.56) * mm, "mid": v(43.38, -23.86) * mm, "end": v(46.68, -25.22) * mm});
            skPoint(sketch, "E93.visualSharp", {"position": v(78.12, -25.22) * mm});
            skArc(sketch, "E93.filletArc", {"start": v(73.46, -25.22) * mm, "mid": v(76.75, -23.86) * mm, "end": v(78.12, -20.56) * mm});
            skLineSegment(sketch, "E94.bottom", {"start": v(-54.92, 22.9) * mm, "end": v(-53.64, 22.9) * mm});
            skLineSegment(sketch, "E94.top", {"start": v(-54.9, 21.84) * mm, "end": v(-53.66, 21.84) * mm});
            skArc(sketch, "E95", {"start": v(-53.64, 22.9) * mm, "mid": v(-53.11, 22.36) * mm, "end": v(-53.66, 21.84) * mm});
            skArc(sketch, "E96", {"start": v(-54.92, 22.9) * mm, "mid": v(-55.44, 22.36) * mm, "end": v(-54.9, 21.84) * mm});
            skPoint(sketch, "E97", {"position": v(-53.11, 22.36) * mm});
            skPoint(sketch, "E98", {"position": v(-55.44, 22.36) * mm});
            skLineSegment(sketch, "E99", {"start": v(-54.92, 22.9) * mm, "end": v(-54.92, 22.37) * mm});
            skLineSegment(sketch, "E100", {"start": v(-53.64, 22.9) * mm, "end": v(-53.64, 22.37) * mm});
            skLineSegment(sketch, "E101.bottom", {"start": v(-54.93, 20.84) * mm, "end": v(-53.65, 20.84) * mm});
            skLineSegment(sketch, "E101.top", {"start": v(-54.92, 19.8) * mm, "end": v(-53.67, 19.8) * mm});
            skArc(sketch, "E102", {"start": v(-53.65, 20.84) * mm, "mid": v(-53.13, 20.3) * mm, "end": v(-53.67, 19.8) * mm});
            skArc(sketch, "E103", {"start": v(-54.93, 20.84) * mm, "mid": v(-55.46, 20.3) * mm, "end": v(-54.92, 19.8) * mm});
            skPoint(sketch, "E104", {"position": v(-53.13, 20.3) * mm});
            skPoint(sketch, "E105", {"position": v(-55.46, 20.3) * mm});
            skLineSegment(sketch, "E106", {"start": v(-54.93, 20.84) * mm, "end": v(-54.93, 20.32) * mm});
            skLineSegment(sketch, "E107", {"start": v(-53.65, 20.84) * mm, "end": v(-53.65, 20.32) * mm});
            skLineSegment(sketch, "E108.bottom", {"start": v(-54.92, 18.8) * mm, "end": v(-53.64, 18.8) * mm});
            skLineSegment(sketch, "E108.top", {"start": v(-54.92, 17.74) * mm, "end": v(-53.64, 17.74) * mm});
            skArc(sketch, "E109", {"start": v(-53.64, 18.8) * mm, "mid": v(-53.11, 18.27) * mm, "end": v(-53.64, 17.74) * mm});
            skArc(sketch, "E110", {"start": v(-54.92, 18.8) * mm, "mid": v(-55.44, 18.27) * mm, "end": v(-54.92, 17.74) * mm});
            skPoint(sketch, "E111", {"position": v(-53.11, 18.27) * mm});
            skPoint(sketch, "E112", {"position": v(-55.44, 18.27) * mm});
            skLineSegment(sketch, "E113", {"start": v(-54.92, 18.8) * mm, "end": v(-54.92, 18.27) * mm});
            skLineSegment(sketch, "E114", {"start": v(-53.64, 18.8) * mm, "end": v(-53.64, 18.27) * mm});
            skLineSegment(sketch, "E115.bottom", {"start": v(-54.9, 16.74) * mm, "end": v(-53.62, 16.74) * mm});
            skLineSegment(sketch, "E115.top", {"start": v(-54.92, 15.7) * mm, "end": v(-53.6, 15.7) * mm});
            skArc(sketch, "E116", {"start": v(-53.62, 16.74) * mm, "mid": v(-53.1, 16.22) * mm, "end": v(-53.6, 15.7) * mm});
            skArc(sketch, "E117", {"start": v(-54.9, 16.74) * mm, "mid": v(-55.43, 16.22) * mm, "end": v(-54.92, 15.7) * mm});
            skPoint(sketch, "E118", {"position": v(-53.1, 16.22) * mm});
            skPoint(sketch, "E119", {"position": v(-55.43, 16.22) * mm});
            skLineSegment(sketch, "E120", {"start": v(-54.9, 16.74) * mm, "end": v(-54.9, 16.22) * mm});
            skLineSegment(sketch, "E121", {"start": v(-53.62, 16.74) * mm, "end": v(-53.62, 16.22) * mm});
            skLineSegment(sketch, "E122", {"start": v(-54.28, 21.84) * mm, "end": v(-54.3, 20.84) * mm});
            skLineSegment(sketch, "E123", {"start": v(-54.3, 19.8) * mm, "end": v(-54.28, 18.8) * mm});
            skLineSegment(sketch, "E124", {"start": v(-54.28, 17.74) * mm, "end": v(-54.26, 16.74) * mm});
            skLineSegment(sketch, "E125", {"start": v(-62.37, 27.09) * mm, "end": v(-62.37, -32.96) * mm});
            skLineSegment(sketch, "E126", {"start": v(-62.37, -32.96) * mm, "end": v(83.98, -32.96) * mm});
            skLineSegment(sketch, "E127", {"start": v(83.98, 27.09) * mm, "end": v(83.98, -32.96) * mm});
            skSolve(sketch);
        }
        {
            var Q0;
            Q0 = qSketchRegion(id + "F0", true);
            var Q1;
            {var subQ0=sQuery(id+"F0.wireOp",EDGE,"E73.right");Q1=makeQuery(id+"F0.imprint","IMPRINT",FACE,{"disambiguationData":[TD([[makeQuery(id+"F0.imprint","IMPRINT",EDGE,{"derivedFrom":subQ0}),1.0]])]});}
            var Q2;
            {var subQ0=sQuery(id+"F0.wireOp",EDGE,"E74.right");Q2=makeQuery(id+"F0.imprint","IMPRINT",FACE,{"disambiguationData":[TD([[makeQuery(id+"F0.imprint","IMPRINT",EDGE,{"derivedFrom":subQ0}),1.0]])]});}
            var Q3;
            {var subQ0=sQuery(id+"F0.wireOp",EDGE,"E75.right");Q3=makeQuery(id+"F0.imprint","IMPRINT",FACE,{"disambiguationData":[TD([[makeQuery(id+"F0.imprint","IMPRINT",EDGE,{"derivedFrom":subQ0}),1.0]])]});}
            var Q4;
            {var subQ0=sQuery(id+"F0.wireOp",EDGE,"E76.right");Q4=makeQuery(id+"F0.imprint","IMPRINT",FACE,{"disambiguationData":[TD([[makeQuery(id+"F0.imprint","IMPRINT",EDGE,{"derivedFrom":subQ0}),1.0]])]});}
            var Q5;
            {var subQ0=sQuery(id+"F0.wireOp",EDGE,"E77.right");Q5=makeQuery(id+"F0.imprint","IMPRINT",FACE,{"disambiguationData":[TD([[makeQuery(id+"F0.imprint","IMPRINT",EDGE,{"derivedFrom":subQ0}),1.0]])]});}
            var Q6;
            {var subQ0=sQuery(id+"F0.wireOp",EDGE,"E78.right");Q6=makeQuery(id+"F0.imprint","IMPRINT",FACE,{"disambiguationData":[TD([[makeQuery(id+"F0.imprint","IMPRINT",EDGE,{"derivedFrom":subQ0}),1.0]])]});}
            var Q7;
            {var subQ0=sQuery(id+"F0.wireOp",EDGE,"E79.right");Q7=makeQuery(id+"F0.imprint","IMPRINT",FACE,{"disambiguationData":[TD([[makeQuery(id+"F0.imprint","IMPRINT",EDGE,{"derivedFrom":subQ0}),1.0]])]});}
            var Q8;
            {var subQ0=sQuery(id+"F0.wireOp",EDGE,"E80.right");Q8=makeQuery(id+"F0.imprint","IMPRINT",FACE,{"disambiguationData":[TD([[makeQuery(id+"F0.imprint","IMPRINT",EDGE,{"derivedFrom":subQ0}),1.0]])]});}
            var Q9;
            {var subQ0=sQuery(id+"F0.wireOp",EDGE,"E81.right");Q9=makeQuery(id+"F0.imprint","IMPRINT",FACE,{"disambiguationData":[TD([[makeQuery(id+"F0.imprint","IMPRINT",EDGE,{"derivedFrom":subQ0}),1.0]])]});}
            var Q10;
            {var subQ0=sQuery(id+"F0.wireOp",EDGE,"E9.right");Q10=makeQuery(id+"F0.imprint","IMPRINT",FACE,{"disambiguationData":[TD([[makeQuery(id+"F0.imprint","IMPRINT",EDGE,{"derivedFrom":subQ0}),1.0]])]});}
            var Q11;
            {var subQ0=sQuery(id+"F0.wireOp",EDGE,"E10.right");Q11=makeQuery(id+"F0.imprint","IMPRINT",FACE,{"disambiguationData":[TD([[makeQuery(id+"F0.imprint","IMPRINT",EDGE,{"derivedFrom":subQ0}),1.0]])]});}
            var Q12;
            {var subQ0=sQuery(id+"F0.wireOp",EDGE,"E8.right");Q12=makeQuery(id+"F0.imprint","IMPRINT",FACE,{"disambiguationData":[TD([[makeQuery(id+"F0.imprint","IMPRINT",EDGE,{"derivedFrom":subQ0}),1.0]])]});}
            var Q13;
            {var subQ0=sQuery(id+"F0.wireOp",EDGE,"E7.right");Q13=makeQuery(id+"F0.imprint","IMPRINT",FACE,{"disambiguationData":[TD([[makeQuery(id+"F0.imprint","IMPRINT",EDGE,{"derivedFrom":subQ0}),1.0]])]});}
            var Q14;
            {var subQ0=sQuery(id+"F0.wireOp",EDGE,"E6.right");Q14=makeQuery(id+"F0.imprint","IMPRINT",FACE,{"disambiguationData":[TD([[makeQuery(id+"F0.imprint","IMPRINT",EDGE,{"derivedFrom":subQ0}),1.0]])]});}
            var Q15;
            {var subQ0=sQuery(id+"F0.wireOp",EDGE,"E5.right");Q15=makeQuery(id+"F0.imprint","IMPRINT",FACE,{"disambiguationData":[TD([[makeQuery(id+"F0.imprint","IMPRINT",EDGE,{"derivedFrom":subQ0}),1.0]])]});}
            var Q16;
            {var subQ0=sQuery(id+"F0.wireOp",EDGE,"E4.right");Q16=makeQuery(id+"F0.imprint","IMPRINT",FACE,{"disambiguationData":[TD([[makeQuery(id+"F0.imprint","IMPRINT",EDGE,{"derivedFrom":subQ0}),1.0]])]});}
            var Q17;
            {var subQ0=sQuery(id+"F0.wireOp",EDGE,"E3.right");Q17=makeQuery(id+"F0.imprint","IMPRINT",FACE,{"disambiguationData":[TD([[makeQuery(id+"F0.imprint","IMPRINT",EDGE,{"derivedFrom":subQ0}),1.0]])]});}
            var Q18;
            {var subQ0=sQuery(id+"F0.wireOp",EDGE,"E2.right");Q18=makeQuery(id+"F0.imprint","IMPRINT",FACE,{"disambiguationData":[TD([[makeQuery(id+"F0.imprint","IMPRINT",EDGE,{"derivedFrom":subQ0}),1.0]])]});}
            var Q19;
            {var subQ0=sQuery(id+"F0.wireOp",EDGE,"E1.right");Q19=makeQuery(id+"F0.imprint","IMPRINT",FACE,{"disambiguationData":[TD([[makeQuery(id+"F0.imprint","IMPRINT",EDGE,{"derivedFrom":subQ0}),1.0]])]});}
            var Q20;
            {var subQ0=sQuery(id+"F0.wireOp",EDGE,"E0.right");Q20=makeQuery(id+"F0.imprint","IMPRINT",FACE,{"disambiguationData":[TD([[makeQuery(id+"F0.imprint","IMPRINT",EDGE,{"derivedFrom":subQ0}),1.0]])]});}
            var Q21;
            {var subQ0=sQuery(id+"F0.wireOp",EDGE,"E14.right");Q21=makeQuery(id+"F0.imprint","IMPRINT",FACE,{"disambiguationData":[TD([[makeQuery(id+"F0.imprint","IMPRINT",EDGE,{"derivedFrom":subQ0}),1.0]])]});}
            var Q22;
            {var subQ0=sQuery(id+"F0.wireOp",EDGE,"E15.right");Q22=makeQuery(id+"F0.imprint","IMPRINT",FACE,{"disambiguationData":[TD([[makeQuery(id+"F0.imprint","IMPRINT",EDGE,{"derivedFrom":subQ0}),1.0]])]});}
            var Q23;
            {var subQ0=sQuery(id+"F0.wireOp",EDGE,"E16.right");Q23=makeQuery(id+"F0.imprint","IMPRINT",FACE,{"disambiguationData":[TD([[makeQuery(id+"F0.imprint","IMPRINT",EDGE,{"derivedFrom":subQ0}),1.0]])]});}
            var Q24;
            {var subQ0=sQuery(id+"F0.wireOp",EDGE,"E17.right");Q24=makeQuery(id+"F0.imprint","IMPRINT",FACE,{"disambiguationData":[TD([[makeQuery(id+"F0.imprint","IMPRINT",EDGE,{"derivedFrom":subQ0}),1.0]])]});}
            var Q25;
            {var subQ0=sQuery(id+"F0.wireOp",EDGE,"E18.right");Q25=makeQuery(id+"F0.imprint","IMPRINT",FACE,{"disambiguationData":[TD([[makeQuery(id+"F0.imprint","IMPRINT",EDGE,{"derivedFrom":subQ0}),1.0]])]});}
            var Q26;
            {var subQ0=sQuery(id+"F0.wireOp",EDGE,"E19.right");Q26=makeQuery(id+"F0.imprint","IMPRINT",FACE,{"disambiguationData":[TD([[makeQuery(id+"F0.imprint","IMPRINT",EDGE,{"derivedFrom":subQ0}),1.0]])]});}
            var Q27;
            {var subQ0=sQuery(id+"F0.wireOp",EDGE,"E20.right");Q27=makeQuery(id+"F0.imprint","IMPRINT",FACE,{"disambiguationData":[TD([[makeQuery(id+"F0.imprint","IMPRINT",EDGE,{"derivedFrom":subQ0}),1.0]])]});}
            var Q28;
            {var subQ0=sQuery(id+"F0.wireOp",EDGE,"E21.right");Q28=makeQuery(id+"F0.imprint","IMPRINT",FACE,{"disambiguationData":[TD([[makeQuery(id+"F0.imprint","IMPRINT",EDGE,{"derivedFrom":subQ0}),1.0]])]});}
            var Q29;
            {var subQ0=sQuery(id+"F0.wireOp",EDGE,"E22.right");Q29=makeQuery(id+"F0.imprint","IMPRINT",FACE,{"disambiguationData":[TD([[makeQuery(id+"F0.imprint","IMPRINT",EDGE,{"derivedFrom":subQ0}),1.0]])]});}
            var Q30;
            {var subQ0=sQuery(id+"F0.wireOp",EDGE,"E23.right");Q30=makeQuery(id+"F0.imprint","IMPRINT",FACE,{"disambiguationData":[TD([[makeQuery(id+"F0.imprint","IMPRINT",EDGE,{"derivedFrom":subQ0}),1.0]])]});}
            var Q31;
            {var subQ0=sQuery(id+"F0.wireOp",EDGE,"E24.right");Q31=makeQuery(id+"F0.imprint","IMPRINT",FACE,{"disambiguationData":[TD([[makeQuery(id+"F0.imprint","IMPRINT",EDGE,{"derivedFrom":subQ0}),1.0]])]});}
            var Q32;
            {var subQ0=sQuery(id+"F0.wireOp",EDGE,"E38.right");Q32=makeQuery(id+"F0.imprint","IMPRINT",FACE,{"disambiguationData":[TD([[makeQuery(id+"F0.imprint","IMPRINT",EDGE,{"derivedFrom":subQ0}),1.0]])]});}
            var Q33;
            {var subQ0=sQuery(id+"F0.wireOp",EDGE,"E37.right");Q33=makeQuery(id+"F0.imprint","IMPRINT",FACE,{"disambiguationData":[TD([[makeQuery(id+"F0.imprint","IMPRINT",EDGE,{"derivedFrom":subQ0}),1.0]])]});}
            var Q34;
            {var subQ0=sQuery(id+"F0.wireOp",EDGE,"E36.right");Q34=makeQuery(id+"F0.imprint","IMPRINT",FACE,{"disambiguationData":[TD([[makeQuery(id+"F0.imprint","IMPRINT",EDGE,{"derivedFrom":subQ0}),1.0]])]});}
            var Q35;
            {var subQ0=sQuery(id+"F0.wireOp",EDGE,"E33.right");Q35=makeQuery(id+"F0.imprint","IMPRINT",FACE,{"disambiguationData":[TD([[makeQuery(id+"F0.imprint","IMPRINT",EDGE,{"derivedFrom":subQ0}),1.0]])]});}
            var Q36;
            {var subQ0=sQuery(id+"F0.wireOp",EDGE,"E32.right");Q36=makeQuery(id+"F0.imprint","IMPRINT",FACE,{"disambiguationData":[TD([[makeQuery(id+"F0.imprint","IMPRINT",EDGE,{"derivedFrom":subQ0}),1.0]])]});}
            var Q37;
            {var subQ0=sQuery(id+"F0.wireOp",EDGE,"E31.right");Q37=makeQuery(id+"F0.imprint","IMPRINT",FACE,{"disambiguationData":[TD([[makeQuery(id+"F0.imprint","IMPRINT",EDGE,{"derivedFrom":subQ0}),1.0]])]});}
            var Q38;
            {var subQ0=sQuery(id+"F0.wireOp",EDGE,"E34.right");Q38=makeQuery(id+"F0.imprint","IMPRINT",FACE,{"disambiguationData":[TD([[makeQuery(id+"F0.imprint","IMPRINT",EDGE,{"derivedFrom":subQ0}),1.0]])]});}
            var Q39;
            {var subQ0=sQuery(id+"F0.wireOp",EDGE,"E35.right");Q39=makeQuery(id+"F0.imprint","IMPRINT",FACE,{"disambiguationData":[TD([[makeQuery(id+"F0.imprint","IMPRINT",EDGE,{"derivedFrom":subQ0}),1.0]])]});}
            var Q40;
            {var subQ0=sQuery(id+"F0.wireOp",EDGE,"E30.right");Q40=makeQuery(id+"F0.imprint","IMPRINT",FACE,{"disambiguationData":[TD([[makeQuery(id+"F0.imprint","IMPRINT",EDGE,{"derivedFrom":subQ0}),1.0]])]});}
            var Q41;
            {var subQ0=sQuery(id+"F0.wireOp",EDGE,"E29.right");Q41=makeQuery(id+"F0.imprint","IMPRINT",FACE,{"disambiguationData":[TD([[makeQuery(id+"F0.imprint","IMPRINT",EDGE,{"derivedFrom":subQ0}),1.0]])]});}
            var Q42;
            {var subQ0=sQuery(id+"F0.wireOp",EDGE,"E28.right");Q42=makeQuery(id+"F0.imprint","IMPRINT",FACE,{"disambiguationData":[TD([[makeQuery(id+"F0.imprint","IMPRINT",EDGE,{"derivedFrom":subQ0}),1.0]])]});}
            var Q43;
            {var subQ0=sQuery(id+"F0.wireOp",EDGE,"E42.right");Q43=makeQuery(id+"F0.imprint","IMPRINT",FACE,{"disambiguationData":[TD([[makeQuery(id+"F0.imprint","IMPRINT",EDGE,{"derivedFrom":subQ0}),1.0]])]});}
            var Q44;
            {var subQ0=sQuery(id+"F0.wireOp",EDGE,"E43.right");Q44=makeQuery(id+"F0.imprint","IMPRINT",FACE,{"disambiguationData":[TD([[makeQuery(id+"F0.imprint","IMPRINT",EDGE,{"derivedFrom":subQ0}),1.0]])]});}
            var Q45;
            {var subQ0=sQuery(id+"F0.wireOp",EDGE,"E44.right");Q45=makeQuery(id+"F0.imprint","IMPRINT",FACE,{"disambiguationData":[TD([[makeQuery(id+"F0.imprint","IMPRINT",EDGE,{"derivedFrom":subQ0}),1.0]])]});}
            var Q46;
            {var subQ0=sQuery(id+"F0.wireOp",EDGE,"E45.right");Q46=makeQuery(id+"F0.imprint","IMPRINT",FACE,{"disambiguationData":[TD([[makeQuery(id+"F0.imprint","IMPRINT",EDGE,{"derivedFrom":subQ0}),1.0]])]});}
            var Q47;
            {var subQ0=sQuery(id+"F0.wireOp",EDGE,"E46.right");Q47=makeQuery(id+"F0.imprint","IMPRINT",FACE,{"disambiguationData":[TD([[makeQuery(id+"F0.imprint","IMPRINT",EDGE,{"derivedFrom":subQ0}),1.0]])]});}
            var Q48;
            {var subQ0=sQuery(id+"F0.wireOp",EDGE,"E47.right");Q48=makeQuery(id+"F0.imprint","IMPRINT",FACE,{"disambiguationData":[TD([[makeQuery(id+"F0.imprint","IMPRINT",EDGE,{"derivedFrom":subQ0}),1.0]])]});}
            var Q49;
            {var subQ0=sQuery(id+"F0.wireOp",EDGE,"E48.right");Q49=makeQuery(id+"F0.imprint","IMPRINT",FACE,{"disambiguationData":[TD([[makeQuery(id+"F0.imprint","IMPRINT",EDGE,{"derivedFrom":subQ0}),1.0]])]});}
            var Q50;
            {var subQ0=sQuery(id+"F0.wireOp",EDGE,"E49.right");Q50=makeQuery(id+"F0.imprint","IMPRINT",FACE,{"disambiguationData":[TD([[makeQuery(id+"F0.imprint","IMPRINT",EDGE,{"derivedFrom":subQ0}),1.0]])]});}
            var Q51;
            {var subQ0=sQuery(id+"F0.wireOp",EDGE,"E50.right");Q51=makeQuery(id+"F0.imprint","IMPRINT",FACE,{"disambiguationData":[TD([[makeQuery(id+"F0.imprint","IMPRINT",EDGE,{"derivedFrom":subQ0}),1.0]])]});}
            var Q52;
            {var subQ0=sQuery(id+"F0.wireOp",EDGE,"E51.right");Q52=makeQuery(id+"F0.imprint","IMPRINT",FACE,{"disambiguationData":[TD([[makeQuery(id+"F0.imprint","IMPRINT",EDGE,{"derivedFrom":subQ0}),1.0]])]});}
            var Q53;
            {var subQ0=sQuery(id+"F0.wireOp",EDGE,"E57.right");Q53=makeQuery(id+"F0.imprint","IMPRINT",FACE,{"disambiguationData":[TD([[makeQuery(id+"F0.imprint","IMPRINT",EDGE,{"derivedFrom":subQ0}),1.0]])]});}
            var Q54;
            {var subQ0=sQuery(id+"F0.wireOp",EDGE,"E58.right");Q54=makeQuery(id+"F0.imprint","IMPRINT",FACE,{"disambiguationData":[TD([[makeQuery(id+"F0.imprint","IMPRINT",EDGE,{"derivedFrom":subQ0}),1.0]])]});}
            var Q55;
            {var subQ0=sQuery(id+"F0.wireOp",EDGE,"E59.right");Q55=makeQuery(id+"F0.imprint","IMPRINT",FACE,{"disambiguationData":[TD([[makeQuery(id+"F0.imprint","IMPRINT",EDGE,{"derivedFrom":subQ0}),1.0]])]});}
            var Q56;
            {var subQ0=sQuery(id+"F0.wireOp",EDGE,"E60.right");Q56=makeQuery(id+"F0.imprint","IMPRINT",FACE,{"disambiguationData":[TD([[makeQuery(id+"F0.imprint","IMPRINT",EDGE,{"derivedFrom":subQ0}),1.0]])]});}
            var Q57;
            {var subQ0=sQuery(id+"F0.wireOp",EDGE,"E61.right");Q57=makeQuery(id+"F0.imprint","IMPRINT",FACE,{"disambiguationData":[TD([[makeQuery(id+"F0.imprint","IMPRINT",EDGE,{"derivedFrom":subQ0}),1.0]])]});}
            var Q58;
            {var subQ0=sQuery(id+"F0.wireOp",EDGE,"E64.right");Q58=makeQuery(id+"F0.imprint","IMPRINT",FACE,{"disambiguationData":[TD([[makeQuery(id+"F0.imprint","IMPRINT",EDGE,{"derivedFrom":subQ0}),1.0]])]});}
            var Q59;
            {var subQ0=sQuery(id+"F0.wireOp",EDGE,"E65.right");Q59=makeQuery(id+"F0.imprint","IMPRINT",FACE,{"disambiguationData":[TD([[makeQuery(id+"F0.imprint","IMPRINT",EDGE,{"derivedFrom":subQ0}),1.0]])]});}
            extrude(context, id + "F1", {"entities" : qUnion([Q0, Q1, Q2, Q3, Q4, Q5, Q6, Q7, Q8, Q9, Q10, Q11, Q12, Q13, Q14, Q15, Q16, Q17, Q18, Q19, Q20, Q21, Q22, Q23, Q24, Q25, Q26, Q27, Q28, Q29, Q30, Q31, Q32, Q33, Q34, Q35, Q36, Q37, Q38, Q39, Q40, Q41, Q42, Q43, Q44, Q45, Q46, Q47, Q48, Q49, Q50, Q51, Q52, Q53, Q54, Q55, Q56, Q57, Q58, Q59]), "depth" : 1 * mm, "offsetDistance" : 25 * mm});
        }
    });
